# Revit family: Distanzrohr
name_source: partatom
category: HLS-Bauteile
revit_build: Autodesk Revit 2017 (Build: 20190508_0315(x64)
units: mm (PartAtom-declared; Revit-internal decimal feet)

## family parameters
Arbeitsebenenbasiert = Ja
Beim Laden mit Abzugskörper schneiden = Nein
Bemaßung runder Anschluss = Durchmesser verwenden
Gemeinsam genutzt = Ja
Immer vertikal = Nein
Raumberechnungspunkt = Nein
Teiletyp = Normal

## types (2) — shared parameters
Fabrikat = MEFA
Firma = MEFA Befestigungs- und Montagesysteme GmbH
Kurztext2 = Länge 2000 mm gvz
Länge = 2000 mm  [stored 6.56168 ft]
Material = Stahl
Mengeneinheit = m
Vorgabe-Ansicht = 1219 mm

## per-type parameters (varying)
| type | Artikelnummer | D | D0 | EAN | Gewicht | Gewinde | Kurztext1 | vpe |
| Distanzrohr 1/2" 2000 mm | 0737002 | 21 mm  [stored 0.0688976 ft] | 16 mm  [stored 0.0524934 ft] | 4250928416957 | 1.13 kg | 1/2'' | Distanzrohr 1/2" | 20 |
| Distanzrohr 1" 2000 mm | 0737004 | 33 mm | 27 mm | 4250928416988 | 2.25 kg | 1'' | Distanzrohr 1" | 10 |

note: [stored X ft] marks values corroborated as IEEE doubles in the binary element streams (Revit-internal decimal feet)
